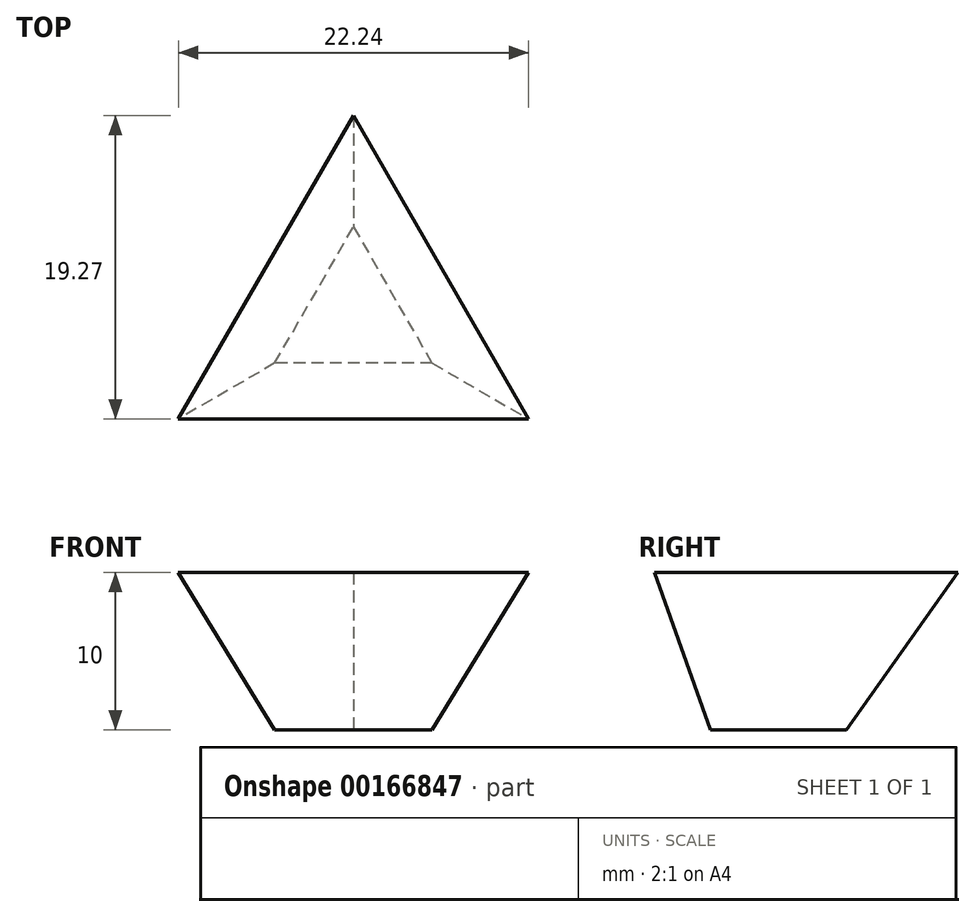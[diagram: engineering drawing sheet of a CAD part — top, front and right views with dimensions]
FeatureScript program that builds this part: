
annotation { "Feature Type Name" : "Feature", "Feature Type Description" : "" }
export const myFeature = defineFeature(function(context is Context, id is Id, definition is map)
    precondition{}
    {
        {
            var Q0;
            Q0=qCreatedBy(makeId("Top.planeOp"),FACE);
            var sketch = newSketch(context, id + "F0", { "sketchPlane" : qUnion([Q0])});
            skLineSegment(sketch, "E0", {"start": v(-5, 0) * mm, "end": v(0, 8.66) * mm});
            skLineSegment(sketch, "E1", {"start": v(0, 8.66) * mm, "end": v(5, 0) * mm});
            skLineSegment(sketch, "E2", {"start": v(-5, 0) * mm, "end": v(5, 0) * mm});
            skSolve(sketch);
        }
        {
            var Q0;
            Q0 = qSketchRegion(id + "F0", true);
            extrude(context, id + "F1", {"entities" : qUnion([Q0]), "depth" : 10 * mm, "hasDraft" : true, "draftAngle" : 90 * degree - atan(2 * (2 ^ 0.5))});
        }
    });
